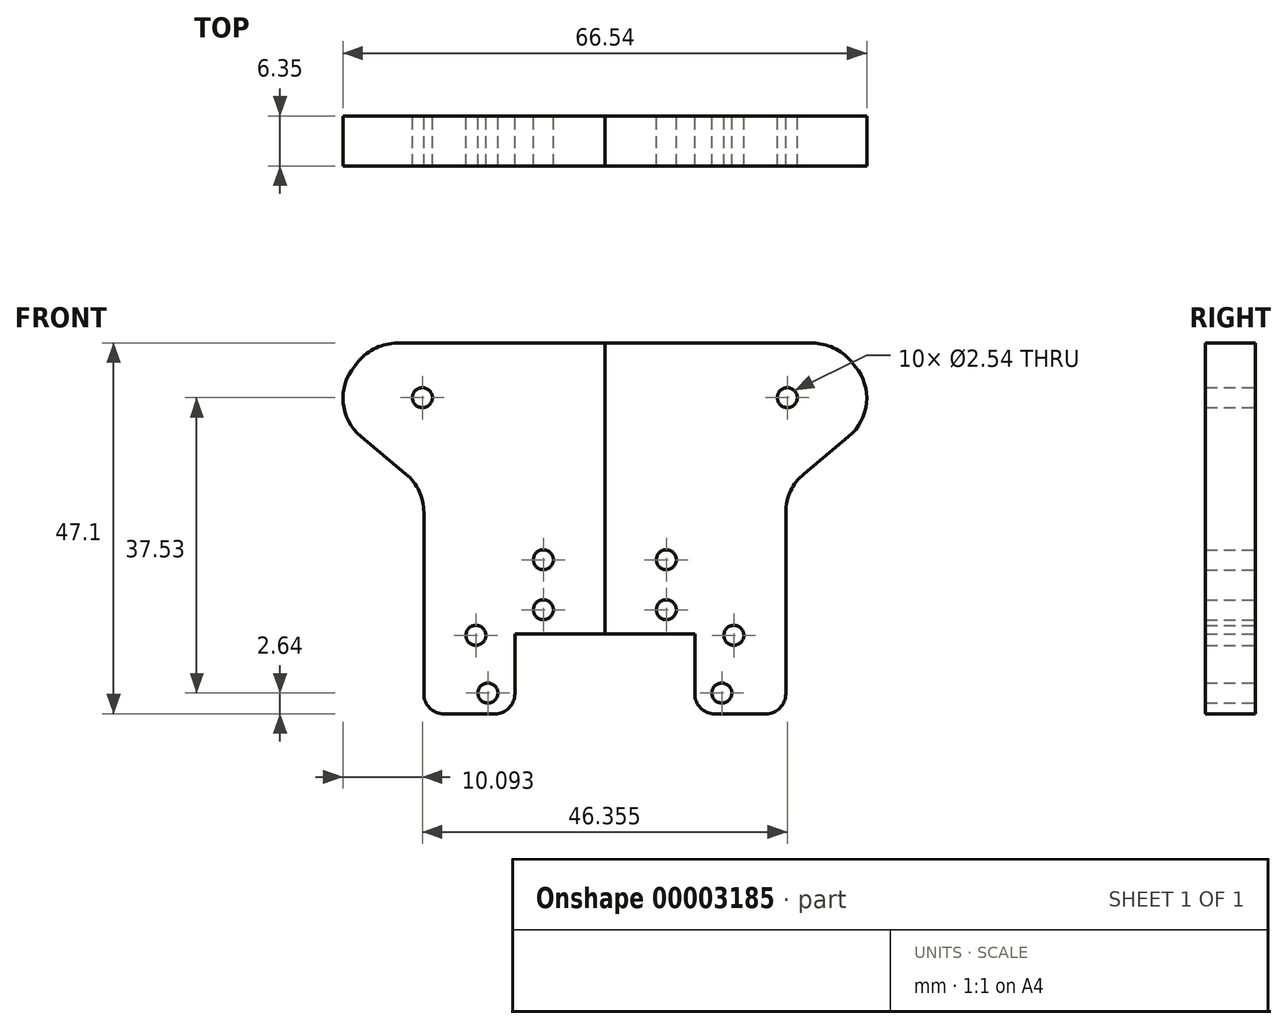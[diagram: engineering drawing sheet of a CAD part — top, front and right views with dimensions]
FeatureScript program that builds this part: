
annotation { "Feature Type Name" : "Feature", "Feature Type Description" : "" }
export const myFeature = defineFeature(function(context is Context, id is Id, definition is map)
    precondition{}
    {
        {
            var Q0;
            Q0=qCreatedBy(makeId("Front.planeOp"),FACE);
            var sketch = newSketch(context, id + "F0", { "sketchPlane" : qUnion([Q0])});
            skLineSegment(sketch, "E0", {"start": v(0, 0) * mm, "end": v(0, 35.2) * mm, "construction": true});
            skCircle(sketch, "E1", {"center": v(-14.86, -20.6) * mm, "radius": 1.27 * mm});
            skCircle(sketch, "E2", {"center": v(-7.81, -10.01) * mm, "radius": 1.27 * mm});
            skCircle(sketch, "E3", {"center": v(-7.81, -3.66) * mm, "radius": 1.27 * mm});
            skLineSegment(sketch, "E4", {"start": v(-7.81, -3.66) * mm, "end": v(-7.81, -10.01) * mm, "construction": true});
            skLineSegment(sketch, "E5.bottom", {"start": v(-19.94, -9.72) * mm, "end": v(-16.38, -9.72) * mm, "construction": true});
            skLineSegment(sketch, "E5.top", {"start": v(-19.94, -13.28) * mm, "end": v(-16.38, -13.28) * mm, "construction": true});
            skLineSegment(sketch, "E5.left", {"start": v(-19.94, -9.72) * mm, "end": v(-19.94, -13.28) * mm, "construction": true});
            skLineSegment(sketch, "E5.right", {"start": v(-16.38, -9.72) * mm, "end": v(-16.38, -13.28) * mm, "construction": true});
            skCircle(sketch, "E6", {"center": v(-16.38, -13.28) * mm, "radius": 1.27 * mm});
            skCircle(sketch, "E7", {"center": v(-23.18, 16.93) * mm, "radius": 1.27 * mm});
            skLineSegment(sketch, "E8", {"start": v(-11.43, -20.7) * mm, "end": v(-11.43, -13.08) * mm});
            skLineSegment(sketch, "E9", {"start": v(-11.43, -13.08) * mm, "end": v(0, -13.08) * mm});
            skLineSegment(sketch, "E10", {"start": v(-13.97, -23.24) * mm, "end": v(-20.45, -23.24) * mm});
            skLineSegment(sketch, "E11", {"start": v(-22.99, -20.7) * mm, "end": v(-22.99, 2.35) * mm});
            skLineSegment(sketch, "E12", {"start": v(-25.28, 7.24) * mm, "end": v(-30.97, 11.97) * mm});
            skLineSegment(sketch, "E13", {"start": v(-31.8, 20.9) * mm, "end": v(-31.26, 21.56) * mm});
            skLineSegment(sketch, "E14", {"start": v(-26.37, 23.86) * mm, "end": v(0, 23.86) * mm});
            skLineSegment(sketch, "E15", {"start": v(0, 23.86) * mm, "end": v(0, -13.08) * mm});
            skPoint(sketch, "E16.visualSharp", {"position": v(-35.86, 16.02) * mm});
            skArc(sketch, "E16.filletArc", {"start": v(-31.8, 20.9) * mm, "mid": v(-33.24, 16.27) * mm, "end": v(-30.97, 11.97) * mm});
            skPoint(sketch, "E17.visualSharp", {"position": v(-29.36, 23.86) * mm});
            skArc(sketch, "E17.filletArc", {"start": v(-26.37, 23.86) * mm, "mid": v(-29.07, 23.25) * mm, "end": v(-31.26, 21.56) * mm});
            skPoint(sketch, "E18.visualSharp", {"position": v(-22.99, 5.33) * mm});
            skArc(sketch, "E18.filletArc", {"start": v(-22.99, 2.35) * mm, "mid": v(-23.59, 5.05) * mm, "end": v(-25.28, 7.24) * mm});
            skPoint(sketch, "E19.visualSharp", {"position": v(-22.99, -23.24) * mm});
            skArc(sketch, "E19.filletArc", {"start": v(-22.99, -20.7) * mm, "mid": v(-22.24, -22.5) * mm, "end": v(-20.45, -23.24) * mm});
            skPoint(sketch, "E20.visualSharp", {"position": v(-11.43, -23.24) * mm});
            skArc(sketch, "E20.filletArc", {"start": v(-13.97, -23.24) * mm, "mid": v(-12.17, -22.5) * mm, "end": v(-11.43, -20.7) * mm});
            skSolve(sketch);
        }
        {
            var Q0;
            Q0=qSketchRegion(id+"F0",true);
            extrude(context, id + "F1", {"entities" : qUnion([Q0]), "depth" : 6.35 * mm});
        }
        {
            var Q0;
            Q0=makeQuery(id+"F1.opExtrude","SWEPT_BODY",BODY,{"disambiguationData":[OSD([sQuery(id+"F0.wireOp",EDGE,"E1"),sQuery(id+"F0.wireOp",EDGE,"E2"),sQuery(id+"F0.wireOp",EDGE,"E3"),sQuery(id+"F0.wireOp",EDGE,"E6"),sQuery(id+"F0.wireOp",EDGE,"E7"),sQuery(id+"F0.wireOp",EDGE,"E8"),sQuery(id+"F0.wireOp",EDGE,"E9"),sQuery(id+"F0.wireOp",EDGE,"E10"),sQuery(id+"F0.wireOp",EDGE,"E11"),sQuery(id+"F0.wireOp",EDGE,"E12"),sQuery(id+"F0.wireOp",EDGE,"E13"),sQuery(id+"F0.wireOp",EDGE,"E14"),sQuery(id+"F0.wireOp",EDGE,"E15"),sQuery(id+"F0.wireOp",EDGE,"E16.filletArc"),sQuery(id+"F0.wireOp",EDGE,"E17.filletArc"),sQuery(id+"F0.wireOp",EDGE,"E18.filletArc"),sQuery(id+"F0.wireOp",EDGE,"E19.filletArc"),sQuery(id+"F0.wireOp",EDGE,"E20.filletArc")])]});
            var Q1;
            Q1=qCreatedBy(makeId("Right.planeOp"),FACE);
            mirror(context, id + "F2", {"entities" : qUnion([Q0]), "mirrorPlane" : qUnion([Q1])});
        }
    });
